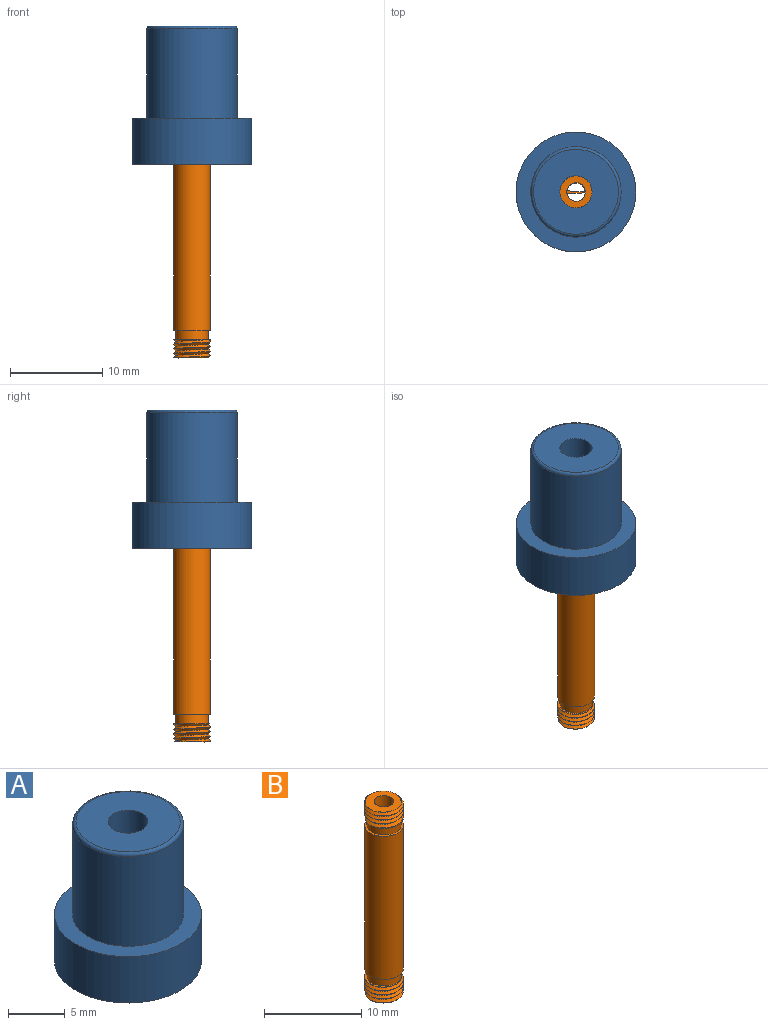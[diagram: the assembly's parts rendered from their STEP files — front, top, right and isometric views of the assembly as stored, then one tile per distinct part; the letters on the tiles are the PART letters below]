
ASSEMBLY  parts=2 mates=1
PART A: 12 faces, bbox 13.2x13.2x15.5 mm
  f0: plane 9.2x9.2mm, normal (0,0,1), area 56.9mm2, adj f1,f11
  f1: cylinder r=1.75mm len=11mm, axis (0,0,1), area 121mm2, adj f0,f2
  f2: plane 3.5x3.5mm, normal (0,0,1), area 0mm2, adj f1,f3
  f3: cylinder r=1.75mm len=4mm, axis (0,0,1), area 5.6mm2, adj f2,f4,f8,f9,f10
  f4: plane 13.21x13.21mm, normal (0,0,-1), area 121.7mm2, adj f3,f5,f9,f10
  f5: cylinder r=6.5mm len=13mm, axis (0,0,1), area 204.2mm2, adj f4,f6
  f6: plane 13x13mm, normal (0,0,1), area 57.3mm2, adj f5,f7
  f7: cylinder r=4.9mm len=9.8mm, axis (0,0,1), area 298.6mm2, adj f6,f11
  f8: plane 0.49x0.25mm, normal (0,-1,0), area 0.1mm2, adj f3,f9,f10
  f9: bspline ~4.62x4.25mm, area 32.1mm2, adj f3,f4,f8,f10
  f10: bspline ~4.62x4.08mm, area 30.1mm2, adj f3,f4,f8,f9
  f11: torus R=4.6mm, axis (0,0,1), area 14.2mm2, adj f0,f7
PART B: 20 faces, bbox 4.2x4.8x25.2 mm
  f0: cylinder r=2mm len=4mm, axis (0,0,1), area 1.1mm2, adj f1,f2,f3,f4,f16
  f1: bspline ~4.62x4mm, area 16.6mm2, adj f0,f2,f3,f4
  f2: plane 4.21x4.09mm, normal (0,0,1), area 2.2mm2, adj f0,f1,f5,f16
  f3: bspline ~4.62x4mm, area 15.6mm2, adj f0,f1,f4,f16
  f4: plane 3.98x3.98mm, normal (0,0,-1), area 7.9mm2, adj f0,f1,f3,f6
  f5: cylinder r=1.75mm len=3.5mm, axis (0,0,1), area 11mm2, adj f2,f7
  f6: cylinder r=1mm len=24mm, axis (0,0,1), area 150.8mm2, adj f4,f8
  f7: plane 4x4mm, normal (0,0,-1), area 2.9mm2, adj f5,f9
  f8: plane 3.98x3.98mm, normal (0,0,1), area 7.9mm2, adj f6,f10,f11,f12
  f9: cylinder r=2mm len=18mm, axis (0,0,1), area 226.2mm2, adj f7,f13
  f10: bspline ~4.62x4mm, area 16.6mm2, adj f8,f11,f12,f14
  f11: bspline ~4.62x4mm, area 15.6mm2, adj f8,f10,f12,f18
  f12: cylinder r=2mm len=4mm, axis (0,0,1), area 0.5mm2, adj f8,f10,f11,f14,f18
  f13: plane 4x4mm, normal (0,0,1), area 2.9mm2, adj f9,f15
  f14: plane 4.21x4.09mm, normal (0,0,-1), area 2.2mm2, adj f10,f12,f15,f18
  f15: cylinder r=1.75mm len=3.5mm, axis (0,0,1), area 11mm2, adj f13,f14
  f16: plane 0.25x0.25mm, normal (0,-1,0), area 0mm2, adj f0,f2,f3
  f17: bspline ~4.62x4mm, area 20.7mm2
  f18: plane 0.25x0.25mm, normal (0,1,0), area 0mm2, adj f11,f12,f14
  f19: bspline ~4.62x4mm, area 20.7mm2
PLACE A t=(-0.01,0,21)mm
PLACE B at identity fixed
MATE fastened A.f1 <-> B.f0  axis (0,0,-1) through (0,0,21)mm
